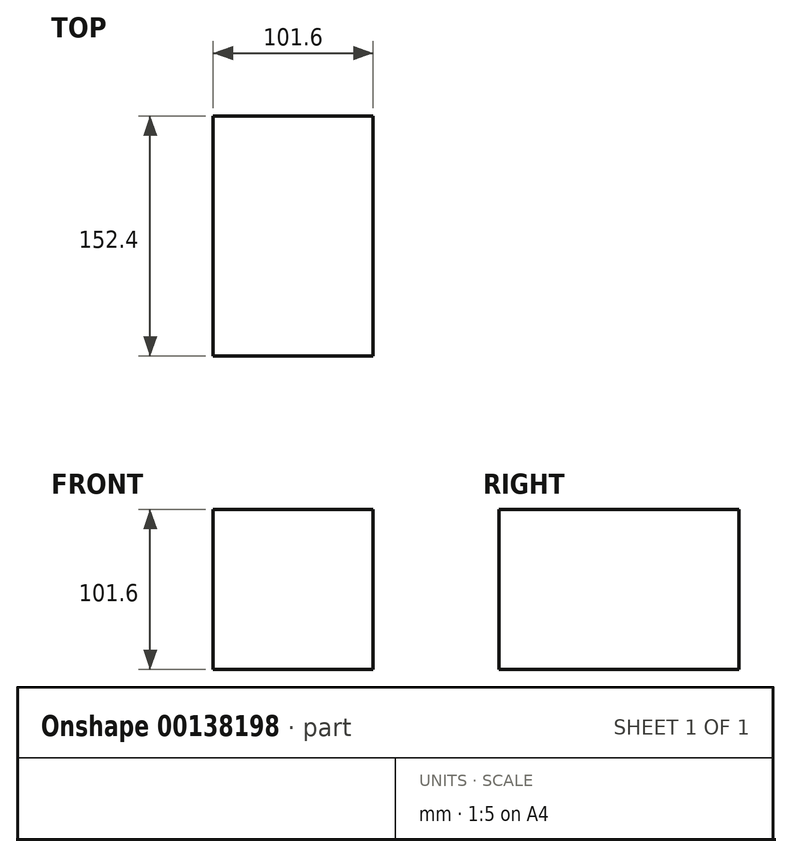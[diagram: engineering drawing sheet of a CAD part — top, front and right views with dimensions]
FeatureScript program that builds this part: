
annotation { "Feature Type Name" : "Feature", "Feature Type Description" : "" }
export const myFeature = defineFeature(function(context is Context, id is Id, definition is map)
    precondition{}
    {
        {
            var Q0;
            Q0=qCreatedBy(makeId("Front.planeOp"),FACE);
            var sketch = newSketch(context, id + "F0", { "sketchPlane" : qUnion([Q0])});
            skLineSegment(sketch, "E0.bottom", {"start": v(0, 0) * mm, "end": v(101.6, 0) * mm});
            skLineSegment(sketch, "E0.top", {"start": v(0, 101.6) * mm, "end": v(101.6, 101.6) * mm});
            skLineSegment(sketch, "E0.left", {"start": v(0, 0) * mm, "end": v(0, 101.6) * mm});
            skLineSegment(sketch, "E0.right", {"start": v(101.6, 0) * mm, "end": v(101.6, 101.6) * mm});
            skSolve(sketch);
        }
        {
            var Q0;
            Q0 = qSketchRegion(id + "F0", true);
            extrude(context, id + "F1", {"entities" : qUnion([Q0]), "depth" : 152.4 * mm});
        }
    });
